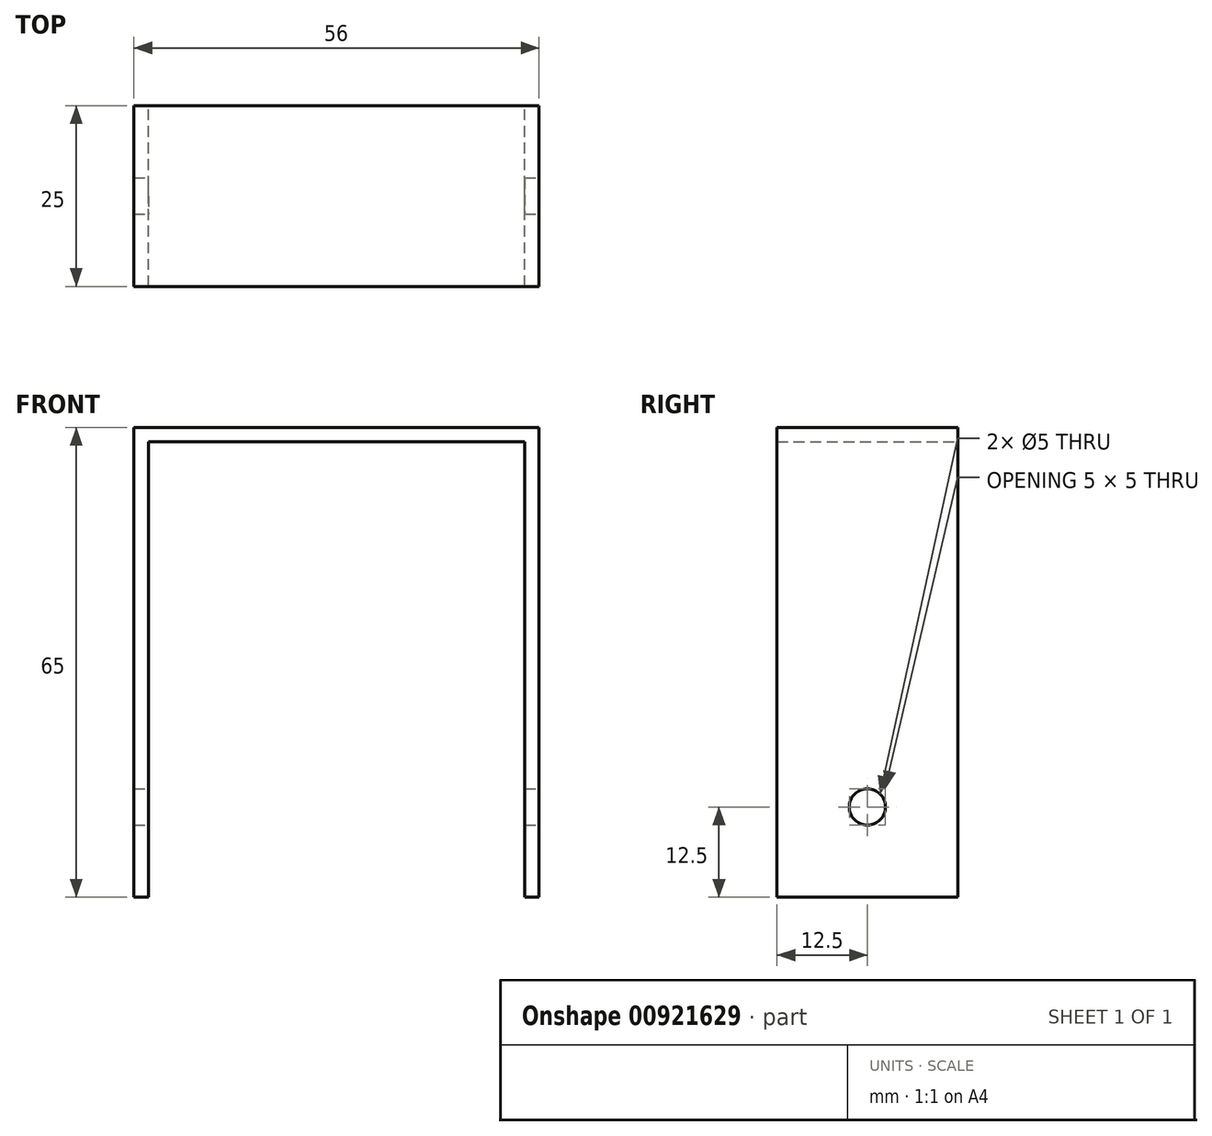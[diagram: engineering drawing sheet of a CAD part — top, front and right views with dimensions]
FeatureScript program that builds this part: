
annotation { "Feature Type Name" : "Feature", "Feature Type Description" : "" }
export const myFeature = defineFeature(function(context is Context, id is Id, definition is map)
    precondition{}
    {
        {
            var Q0;
            Q0=qCreatedBy(makeId("Front.planeOp"),FACE);
            var sketch = newSketch(context, id + "F0", { "sketchPlane" : qUnion([Q0])});
            skLineSegment(sketch, "E0", {"start": v(0, -65) * mm, "end": v(0, 0) * mm});
            skLineSegment(sketch, "E1", {"start": v(0, 0) * mm, "end": v(-56, 0) * mm});
            skLineSegment(sketch, "E2", {"start": v(-56, 0) * mm, "end": v(-56, -65) * mm});
            skLineSegment(sketch, "E3", {"start": v(-56, -65) * mm, "end": v(-54, -65) * mm});
            skLineSegment(sketch, "E4", {"start": v(-54, -65) * mm, "end": v(-54, -2) * mm});
            skLineSegment(sketch, "E5", {"start": v(-54, -2) * mm, "end": v(-2, -2) * mm});
            skLineSegment(sketch, "E6", {"start": v(-2, -2) * mm, "end": v(-2, -65) * mm});
            skLineSegment(sketch, "E7", {"start": v(-2, -65) * mm, "end": v(0, -65) * mm});
            skLineSegment(sketch, "E8", {"start": v(-54, -2) * mm, "end": v(-54, 0) * mm, "construction": true});
            skSolve(sketch);
        }
        {
            var Q0;
            Q0 = qSketchRegion(id + "F0", true);
            extrude(context, id + "F1", {"entities" : qUnion([Q0]), "endBound" : BoundingType.SYMMETRIC, "depth" : 25 * mm, "offsetDistance" : 25 * mm});
        }
        {
            var Q0;
            Q0=qCreatedBy(makeId("Right.planeOp"),FACE);
            var sketch = newSketch(context, id + "F2", { "sketchPlane" : qUnion([Q0])});
            skCircle(sketch, "E9", {"center": v(0, -52.5) * mm, "radius": 2.5 * mm});
            skSolve(sketch);
        }
        {
            var Q0;
            Q0 = qSketchRegion(id + "F2", true);
            extrude(context, id + "F3", {"entities" : qUnion([Q0]), "operationType" : NewBodyOperationType.REMOVE, "endBound" : BoundingType.THROUGH_ALL, "oppositeDirection" : true, "depth" : 25 * mm, "offsetDistance" : 25 * mm, "hasSecondDirection" : true, "secondDirectionBound" : SecondDirectionBoundingType.THROUGH_ALL, "secondDirectionOppositeDirection" : false, "secondDirectionDepth" : 25 * mm});
        }
    });
